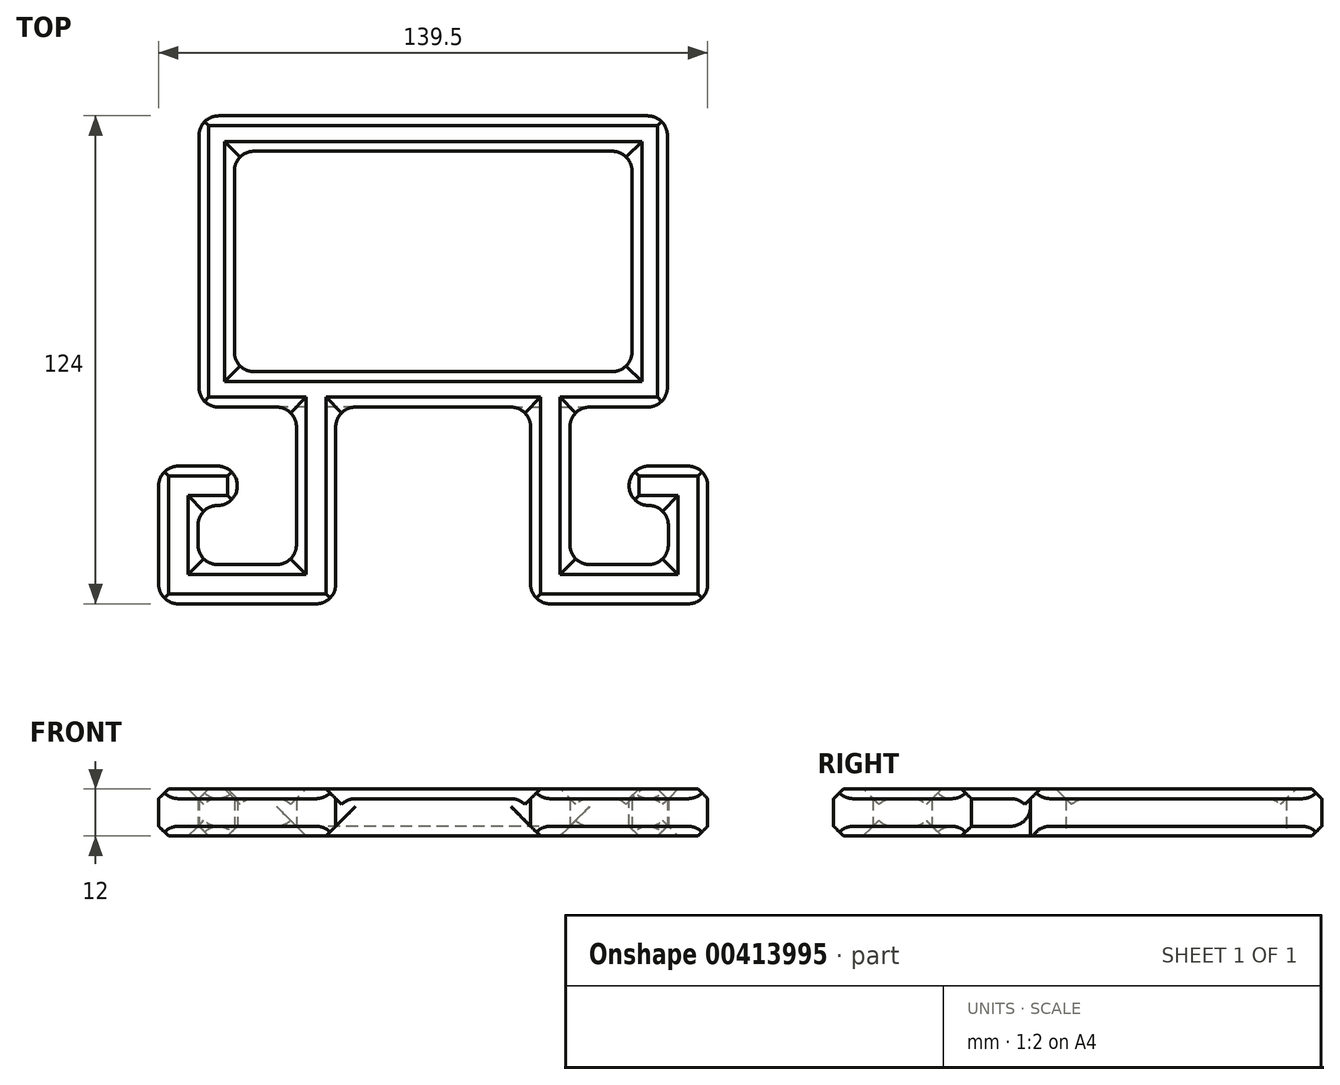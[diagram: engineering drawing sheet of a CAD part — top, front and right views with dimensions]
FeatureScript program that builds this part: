
annotation { "Feature Type Name" : "Feature", "Feature Type Description" : "" }
export const myFeature = defineFeature(function(context is Context, id is Id, definition is map)
    precondition{}
    {
        {
            var Q0;
            Q0=qCreatedBy(makeId("Top.planeOp"),FACE);
            var sketch = newSketch(context, id + "F0", { "sketchPlane" : qUnion([Q0])});
            skLineSegment(sketch, "E0.bottom", {"start": v(-43.9, 82.34) * mm, "end": v(75.1, 82.34) * mm});
            skLineSegment(sketch, "E0.top", {"start": v(-43.9, 8.34) * mm, "end": v(75.1, 8.34) * mm});
            skLineSegment(sketch, "E0.left", {"start": v(-43.9, 82.34) * mm, "end": v(-43.9, 8.34) * mm});
            skLineSegment(sketch, "E0.right", {"start": v(75.1, 82.34) * mm, "end": v(75.1, 8.34) * mm});
            skLineSegment(sketch, "E1.0", {"start": v(-34.9, 73.34) * mm, "end": v(66.1, 73.34) * mm});
            skLineSegment(sketch, "E1.1", {"start": v(-34.9, 73.34) * mm, "end": v(-34.9, 17.34) * mm});
            skLineSegment(sketch, "E1.2", {"start": v(-34.9, 17.34) * mm, "end": v(66.1, 17.34) * mm});
            skLineSegment(sketch, "E1.3", {"start": v(66.1, 73.34) * mm, "end": v(66.1, 17.34) * mm});
            skPoint(sketch, "E2", {"position": v(15.6, 8.34) * mm});
            skLineSegment(sketch, "E3", {"start": v(-43.9, 8.34) * mm, "end": v(15.6, 8.34) * mm});
            skLineSegment(sketch, "E4", {"start": v(15.6, 8.34) * mm, "end": v(75.1, 8.34) * mm});
            skPoint(sketch, "E5", {"position": v(-14.15, 8.34) * mm});
            skPoint(sketch, "E6", {"position": v(45.35, 8.34) * mm});
            skLineSegment(sketch, "E7", {"start": v(15.6, 8.34) * mm, "end": v(15.6, -50.56) * mm, "construction": true});
            skLineSegment(sketch, "E8", {"start": v(-9.15, 8.34) * mm, "end": v(-9.15, -41.66) * mm});
            skLineSegment(sketch, "E9", {"start": v(-9.15, -41.66) * mm, "end": v(-54.15, -41.66) * mm});
            skLineSegment(sketch, "E10", {"start": v(-54.15, -41.66) * mm, "end": v(-54.15, -6.66) * mm});
            skLineSegment(sketch, "E11", {"start": v(-54.15, -6.66) * mm, "end": v(-44.15, -6.66) * mm});
            skLineSegment(sketch, "E12", {"start": v(-44.15, -16.66) * mm, "end": v(-44.15, -31.66) * mm});
            skLineSegment(sketch, "E13", {"start": v(-19.15, -31.66) * mm, "end": v(-19.15, 8.34) * mm});
            skLineSegment(sketch, "E14", {"start": v(-44.15, -31.66) * mm, "end": v(-19.15, -31.66) * mm});
            skLineSegment(sketch, "E15", {"start": v(-44.15, -16.66) * mm, "end": v(-34.15, -16.66) * mm});
            skLineSegment(sketch, "E16", {"start": v(-34.15, -16.66) * mm, "end": v(-34.15, -6.66) * mm});
            skLineSegment(sketch, "E17", {"start": v(-34.15, -6.66) * mm, "end": v(-44.15, -6.66) * mm});
            skLineSegment(sketch, "E18.MirrorCS", {"start": v(50.35, -31.66) * mm, "end": v(50.35, 8.34) * mm});
            skLineSegment(sketch, "E19.MirrorCS", {"start": v(40.35, 8.34) * mm, "end": v(40.35, -41.66) * mm});
            skLineSegment(sketch, "E20.MirrorCS", {"start": v(40.35, -41.66) * mm, "end": v(85.35, -41.66) * mm});
            skLineSegment(sketch, "E21.MirrorCS", {"start": v(75.35, -31.66) * mm, "end": v(50.35, -31.66) * mm});
            skLineSegment(sketch, "E22.MirrorCS", {"start": v(75.35, -16.66) * mm, "end": v(65.35, -16.66) * mm});
            skLineSegment(sketch, "E23.MirrorCS", {"start": v(75.35, -16.66) * mm, "end": v(75.35, -31.66) * mm});
            skLineSegment(sketch, "E24.MirrorCS", {"start": v(65.35, -16.66) * mm, "end": v(65.35, -6.66) * mm});
            skLineSegment(sketch, "E25.MirrorCS", {"start": v(65.35, -6.66) * mm, "end": v(75.35, -6.66) * mm});
            skLineSegment(sketch, "E26.MirrorCS", {"start": v(85.35, -6.66) * mm, "end": v(75.35, -6.66) * mm});
            skLineSegment(sketch, "E27.MirrorCS", {"start": v(85.35, -41.66) * mm, "end": v(85.35, -6.66) * mm});
            skSolve(sketch);
        }
        {
            var Q0;
            Q0=makeQuery(id+"F0.imprint","IMPRINT",FACE,{"disambiguationData":[TD([[makeQuery(id+"F0.imprint","IMPRINT",EDGE,{"derivedFrom":sQuery(id+"F0.wireOp",EDGE,"E0.bottom")}),-1.0]])]});
            var Q1;
            {var subQ1=sQuery(id+"F0.wireOp",EDGE,"E8");Q1=makeQuery(id+"F0.imprint","IMPRINT",FACE,{"disambiguationData":[TD([[makeQuery(id+"F0.imprint","IMPRINT",EDGE,{"derivedFrom":subQ1}),-1.0]])]});}
            var Q2;
            {var subQ0=sQuery(id+"F0.wireOp",EDGE,"E18.MirrorCS");Q2=makeQuery(id+"F0.imprint","IMPRINT",FACE,{"disambiguationData":[TD([[makeQuery(id+"F0.imprint","IMPRINT",EDGE,{"derivedFrom":subQ0}),1.0]])]});}
            extrude(context, id + "F1", {"entities" : qUnion([Q0, Q1, Q2]), "depth" : 12 * mm});
        }
        {
            var Q0;
            Q0=makeQuery(id+"F1.opExtrude","CAP_EDGE",EDGE,{"disambiguationData":[OSD([sQuery(id+"F0.wireOp",EDGE,"E0.left")])],"isStart":true});
            var Q1;
            Q1=makeQuery(id+"F1.opExtrude","CAP_EDGE",EDGE,{"disambiguationData":[OSD([sQuery(id+"F0.wireOp",EDGE,"E0.bottom")])],"isStart":true});
            var Q2;
            Q2=makeQuery(id+"F1.opExtrude","CAP_EDGE",EDGE,{"disambiguationData":[OSD([sQuery(id+"F0.wireOp",EDGE,"E0.right")])],"isStart":true});
            var Q3;
            Q3=makeQuery(id+"F1.opExtrude","CAP_EDGE",EDGE,{"disambiguationData":[OSD([sQuery(id+"F0.wireOp",EDGE,"E4")])],"isStart":true});
            var Q4;
            Q4=makeQuery(id+"F1.opExtrude","CAP_EDGE",EDGE,{"disambiguationData":[OSD([sQuery(id+"F0.wireOp",EDGE,"E18.MirrorCS")])],"isStart":true});
            var Q5;
            Q5=makeQuery(id+"F1.opExtrude","CAP_EDGE",EDGE,{"disambiguationData":[OSD([sQuery(id+"F0.wireOp",EDGE,"E21.MirrorCS")])],"isStart":true});
            var Q6;
            Q6=makeQuery(id+"F1.opExtrude","CAP_EDGE",EDGE,{"disambiguationData":[OSD([sQuery(id+"F0.wireOp",EDGE,"E23.MirrorCS")])],"isStart":true});
            var Q7;
            Q7=makeQuery(id+"F1.opExtrude","CAP_EDGE",EDGE,{"disambiguationData":[OSD([sQuery(id+"F0.wireOp",EDGE,"E22.MirrorCS")])],"isStart":true});
            var Q8;
            Q8=makeQuery(id+"F1.opExtrude","CAP_EDGE",EDGE,{"disambiguationData":[OSD([sQuery(id+"F0.wireOp",EDGE,"E24.MirrorCS")])],"isStart":true});
            var Q9;
            Q9=makeQuery(id+"F1.opExtrude","CAP_EDGE",EDGE,{"disambiguationData":[OSD([sQuery(id+"F0.wireOp",EDGE,"E25.MirrorCS"),sQuery(id+"F0.wireOp",EDGE,"E26.MirrorCS")])],"isStart":true});
            var Q10;
            Q10=makeQuery(id+"F1.opExtrude","CAP_EDGE",EDGE,{"disambiguationData":[OSD([sQuery(id+"F0.wireOp",EDGE,"E27.MirrorCS")])],"isStart":true});
            var Q11;
            Q11=makeQuery(id+"F1.opExtrude","CAP_EDGE",EDGE,{"disambiguationData":[OSD([sQuery(id+"F0.wireOp",EDGE,"E20.MirrorCS")])],"isStart":true});
            var Q12;
            Q12=makeQuery(id+"F1.opExtrude","CAP_EDGE",EDGE,{"disambiguationData":[OSD([sQuery(id+"F0.wireOp",EDGE,"E3"),sQuery(id+"F0.wireOp",EDGE,"E4")])],"isStart":true});
            var Q13;
            Q13=makeQuery(id+"F1.opExtrude","CAP_EDGE",EDGE,{"disambiguationData":[OSD([sQuery(id+"F0.wireOp",EDGE,"E19.MirrorCS")])],"isStart":true});
            var Q14;
            Q14=makeQuery(id+"F1.opExtrude","CAP_EDGE",EDGE,{"disambiguationData":[OSD([sQuery(id+"F0.wireOp",EDGE,"E8")])],"isStart":true});
            var Q15;
            Q15=makeQuery(id+"F1.opExtrude","CAP_EDGE",EDGE,{"disambiguationData":[OSD([sQuery(id+"F0.wireOp",EDGE,"E9")])],"isStart":true});
            var Q16;
            Q16=makeQuery(id+"F1.opExtrude","CAP_EDGE",EDGE,{"disambiguationData":[OSD([sQuery(id+"F0.wireOp",EDGE,"E10")])],"isStart":true});
            var Q17;
            Q17=makeQuery(id+"F1.opExtrude","CAP_EDGE",EDGE,{"disambiguationData":[OSD([sQuery(id+"F0.wireOp",EDGE,"E11"),sQuery(id+"F0.wireOp",EDGE,"E17")])],"isStart":true});
            var Q18;
            Q18=makeQuery(id+"F1.opExtrude","CAP_EDGE",EDGE,{"disambiguationData":[OSD([sQuery(id+"F0.wireOp",EDGE,"E14")])],"isStart":true});
            var Q19;
            Q19=makeQuery(id+"F1.opExtrude","CAP_EDGE",EDGE,{"disambiguationData":[OSD([sQuery(id+"F0.wireOp",EDGE,"E13")])],"isStart":true});
            var Q20;
            Q20=makeQuery(id+"F1.opExtrude","CAP_EDGE",EDGE,{"disambiguationData":[OSD([sQuery(id+"F0.wireOp",EDGE,"E3")])],"isStart":true});
            var Q21;
            Q21=makeQuery(id+"F1.opExtrude","CAP_EDGE",EDGE,{"disambiguationData":[OSD([sQuery(id+"F0.wireOp",EDGE,"E3"),sQuery(id+"F0.wireOp",EDGE,"E4")])],"isStart":false});
            var Q22;
            Q22=makeQuery(id+"F1.opExtrude","CAP_FACE",FACE,{"disambiguationData":[OSD([sQuery(id+"F0.wireOp",EDGE,"E0.bottom"),sQuery(id+"F0.wireOp",EDGE,"E0.left"),sQuery(id+"F0.wireOp",EDGE,"E0.right"),sQuery(id+"F0.wireOp",EDGE,"E1.0"),sQuery(id+"F0.wireOp",EDGE,"E1.1"),sQuery(id+"F0.wireOp",EDGE,"E1.2"),sQuery(id+"F0.wireOp",EDGE,"E1.3"),sQuery(id+"F0.wireOp",EDGE,"E3"),sQuery(id+"F0.wireOp",EDGE,"E4"),sQuery(id+"F0.wireOp",EDGE,"E8"),sQuery(id+"F0.wireOp",EDGE,"E9"),sQuery(id+"F0.wireOp",EDGE,"E10"),sQuery(id+"F0.wireOp",EDGE,"E11"),sQuery(id+"F0.wireOp",EDGE,"E12"),sQuery(id+"F0.wireOp",EDGE,"E13"),sQuery(id+"F0.wireOp",EDGE,"E14"),sQuery(id+"F0.wireOp",EDGE,"E15"),sQuery(id+"F0.wireOp",EDGE,"E16"),sQuery(id+"F0.wireOp",EDGE,"E17"),sQuery(id+"F0.wireOp",EDGE,"E18.MirrorCS"),sQuery(id+"F0.wireOp",EDGE,"E19.MirrorCS"),sQuery(id+"F0.wireOp",EDGE,"E20.MirrorCS"),sQuery(id+"F0.wireOp",EDGE,"E21.MirrorCS"),sQuery(id+"F0.wireOp",EDGE,"E22.MirrorCS"),sQuery(id+"F0.wireOp",EDGE,"E23.MirrorCS"),sQuery(id+"F0.wireOp",EDGE,"E24.MirrorCS"),sQuery(id+"F0.wireOp",EDGE,"E25.MirrorCS"),sQuery(id+"F0.wireOp",EDGE,"E26.MirrorCS"),sQuery(id+"F0.wireOp",EDGE,"E27.MirrorCS")])],"isStart":false});
            var Q23;
            Q23=makeQuery(id+"F1.opExtrude","CAP_EDGE",EDGE,{"disambiguationData":[OSD([sQuery(id+"F0.wireOp",EDGE,"E15")])],"isStart":true});
            var Q24;
            Q24=makeQuery(id+"F1.opExtrude","CAP_EDGE",EDGE,{"disambiguationData":[OSD([sQuery(id+"F0.wireOp",EDGE,"E12")])],"isStart":true});
            var Q25;
            Q25=makeQuery(id+"F1.opExtrude","CAP_EDGE",EDGE,{"disambiguationData":[OSD([sQuery(id+"F0.wireOp",EDGE,"E16")])],"isStart":true});
            chamfer(context, id + "F2", {"entities" : qUnion([Q0, Q1, Q2, Q3, Q4, Q5, Q6, Q7, Q8, Q9, Q10, Q11, Q12, Q13, Q14, Q15, Q16, Q17, Q18, Q19, Q20, Q21, Q22, Q23, Q24, Q25]), "width" : 2.5 * mm, "tangentPropagation" : true});
        }
        {
            var Q0;
            Q0=makeQuery(id+"F1.opExtrude","SWEPT_EDGE",EDGE,{"disambiguationData":[OSD([sQuery(id+"F0.wireOp",EDGE,"E1.0"),sQuery(id+"F0.wireOp",EDGE,"E1.1")])]});
            var Q1;
            Q1=makeQuery(id+"F1.opExtrude","SWEPT_EDGE",EDGE,{"disambiguationData":[OSD([sQuery(id+"F0.wireOp",EDGE,"E1.1"),sQuery(id+"F0.wireOp",EDGE,"E1.2")])]});
            var Q2;
            Q2=makeQuery(id+"F1.opExtrude","SWEPT_EDGE",EDGE,{"disambiguationData":[OSD([sQuery(id+"F0.wireOp",EDGE,"E1.2"),sQuery(id+"F0.wireOp",EDGE,"E1.3")])]});
            var Q3;
            Q3=makeQuery(id+"F1.opExtrude","SWEPT_EDGE",EDGE,{"disambiguationData":[OSD([sQuery(id+"F0.wireOp",EDGE,"E1.0"),sQuery(id+"F0.wireOp",EDGE,"E1.3")])]});
            var Q4;
            Q4=makeQuery(id+"F1.opExtrude","SWEPT_EDGE",EDGE,{"disambiguationData":[OSD([sQuery(id+"F0.wireOp",EDGE,"E0.right"),sQuery(id+"F0.wireOp",EDGE,"E4")])]});
            var Q5;
            Q5=makeQuery(id+"F1.opExtrude","SWEPT_EDGE",EDGE,{"disambiguationData":[OSD([sQuery(id+"F0.wireOp",EDGE,"E0.left"),sQuery(id+"F0.wireOp",EDGE,"E3")])]});
            var Q6;
            Q6=makeQuery(id+"F1.opExtrude","SWEPT_EDGE",EDGE,{"disambiguationData":[OSD([sQuery(id+"F0.wireOp",EDGE,"E0.bottom"),sQuery(id+"F0.wireOp",EDGE,"E0.left")])]});
            var Q7;
            Q7=makeQuery(id+"F1.opExtrude","SWEPT_EDGE",EDGE,{"disambiguationData":[OSD([sQuery(id+"F0.wireOp",EDGE,"E0.bottom"),sQuery(id+"F0.wireOp",EDGE,"E0.right")])]});
            var Q8;
            Q8=makeQuery(id+"F1.opExtrude","SWEPT_EDGE",EDGE,{"disambiguationData":[OSD([sQuery(id+"F0.wireOp",EDGE,"E3"),sQuery(id+"F0.wireOp",EDGE,"E13")])]});
            var Q9;
            Q9=makeQuery(id+"F1.opExtrude","SWEPT_EDGE",EDGE,{"disambiguationData":[OSD([sQuery(id+"F0.wireOp",EDGE,"E3"),sQuery(id+"F0.wireOp",EDGE,"E8")])]});
            var Q10;
            Q10=makeQuery(id+"F1.opExtrude","SWEPT_EDGE",EDGE,{"disambiguationData":[OSD([sQuery(id+"F0.wireOp",EDGE,"E4"),sQuery(id+"F0.wireOp",EDGE,"E19.MirrorCS")])]});
            var Q11;
            Q11=makeQuery(id+"F1.opExtrude","SWEPT_EDGE",EDGE,{"disambiguationData":[OSD([sQuery(id+"F0.wireOp",EDGE,"E4"),sQuery(id+"F0.wireOp",EDGE,"E18.MirrorCS")])]});
            var Q12;
            Q12=makeQuery(id+"F1.opExtrude","SWEPT_EDGE",EDGE,{"disambiguationData":[OSD([sQuery(id+"F0.wireOp",EDGE,"E8"),sQuery(id+"F0.wireOp",EDGE,"E9")])]});
            var Q13;
            Q13=makeQuery(id+"F1.opExtrude","SWEPT_EDGE",EDGE,{"disambiguationData":[OSD([sQuery(id+"F0.wireOp",EDGE,"E9"),sQuery(id+"F0.wireOp",EDGE,"E10")])]});
            var Q14;
            Q14=makeQuery(id+"F1.opExtrude","SWEPT_EDGE",EDGE,{"disambiguationData":[OSD([sQuery(id+"F0.wireOp",EDGE,"E10"),sQuery(id+"F0.wireOp",EDGE,"E11")])]});
            var Q15;
            Q15=makeQuery(id+"F1.opExtrude","SWEPT_EDGE",EDGE,{"disambiguationData":[OSD([sQuery(id+"F0.wireOp",EDGE,"E16"),sQuery(id+"F0.wireOp",EDGE,"E17")])]});
            var Q16;
            Q16=makeQuery(id+"F1.opExtrude","SWEPT_EDGE",EDGE,{"disambiguationData":[OSD([sQuery(id+"F0.wireOp",EDGE,"E15"),sQuery(id+"F0.wireOp",EDGE,"E16")])]});
            var Q17;
            Q17=makeQuery(id+"F1.opExtrude","SWEPT_EDGE",EDGE,{"disambiguationData":[OSD([sQuery(id+"F0.wireOp",EDGE,"E12"),sQuery(id+"F0.wireOp",EDGE,"E15")])]});
            var Q18;
            Q18=makeQuery(id+"F1.opExtrude","SWEPT_EDGE",EDGE,{"disambiguationData":[OSD([sQuery(id+"F0.wireOp",EDGE,"E12"),sQuery(id+"F0.wireOp",EDGE,"E14")])]});
            var Q19;
            Q19=makeQuery(id+"F1.opExtrude","SWEPT_EDGE",EDGE,{"disambiguationData":[OSD([sQuery(id+"F0.wireOp",EDGE,"E13"),sQuery(id+"F0.wireOp",EDGE,"E14")])]});
            var Q20;
            Q20=makeQuery(id+"F1.opExtrude","SWEPT_EDGE",EDGE,{"disambiguationData":[OSD([sQuery(id+"F0.wireOp",EDGE,"E19.MirrorCS"),sQuery(id+"F0.wireOp",EDGE,"E20.MirrorCS")])]});
            var Q21;
            Q21=makeQuery(id+"F1.opExtrude","SWEPT_EDGE",EDGE,{"disambiguationData":[OSD([sQuery(id+"F0.wireOp",EDGE,"E20.MirrorCS"),sQuery(id+"F0.wireOp",EDGE,"E27.MirrorCS")])]});
            var Q22;
            Q22=makeQuery(id+"F1.opExtrude","SWEPT_EDGE",EDGE,{"disambiguationData":[OSD([sQuery(id+"F0.wireOp",EDGE,"E26.MirrorCS"),sQuery(id+"F0.wireOp",EDGE,"E27.MirrorCS")])]});
            var Q23;
            Q23=makeQuery(id+"F1.opExtrude","SWEPT_EDGE",EDGE,{"disambiguationData":[OSD([sQuery(id+"F0.wireOp",EDGE,"E24.MirrorCS"),sQuery(id+"F0.wireOp",EDGE,"E25.MirrorCS")])]});
            var Q24;
            Q24=makeQuery(id+"F1.opExtrude","SWEPT_EDGE",EDGE,{"disambiguationData":[OSD([sQuery(id+"F0.wireOp",EDGE,"E22.MirrorCS"),sQuery(id+"F0.wireOp",EDGE,"E24.MirrorCS")])]});
            var Q25;
            Q25=makeQuery(id+"F1.opExtrude","SWEPT_EDGE",EDGE,{"disambiguationData":[OSD([sQuery(id+"F0.wireOp",EDGE,"E22.MirrorCS"),sQuery(id+"F0.wireOp",EDGE,"E23.MirrorCS")])]});
            var Q26;
            Q26=makeQuery(id+"F1.opExtrude","SWEPT_EDGE",EDGE,{"disambiguationData":[OSD([sQuery(id+"F0.wireOp",EDGE,"E18.MirrorCS"),sQuery(id+"F0.wireOp",EDGE,"E21.MirrorCS")])]});
            var Q27;
            Q27=makeQuery(id+"F1.opExtrude","SWEPT_EDGE",EDGE,{"disambiguationData":[OSD([sQuery(id+"F0.wireOp",EDGE,"E21.MirrorCS"),sQuery(id+"F0.wireOp",EDGE,"E23.MirrorCS")])]});
            fillet(context, id + "F3", {"entities" : qUnion([Q0, Q1, Q2, Q3, Q4, Q5, Q6, Q7, Q8, Q9, Q10, Q11, Q12, Q13, Q14, Q15, Q16, Q17, Q18, Q19, Q20, Q21, Q22, Q23, Q24, Q25, Q26, Q27]), "radius" : 5 * mm, "tangentPropagation" : true, "allowEdgeOverflow" : false});
        }
    });
